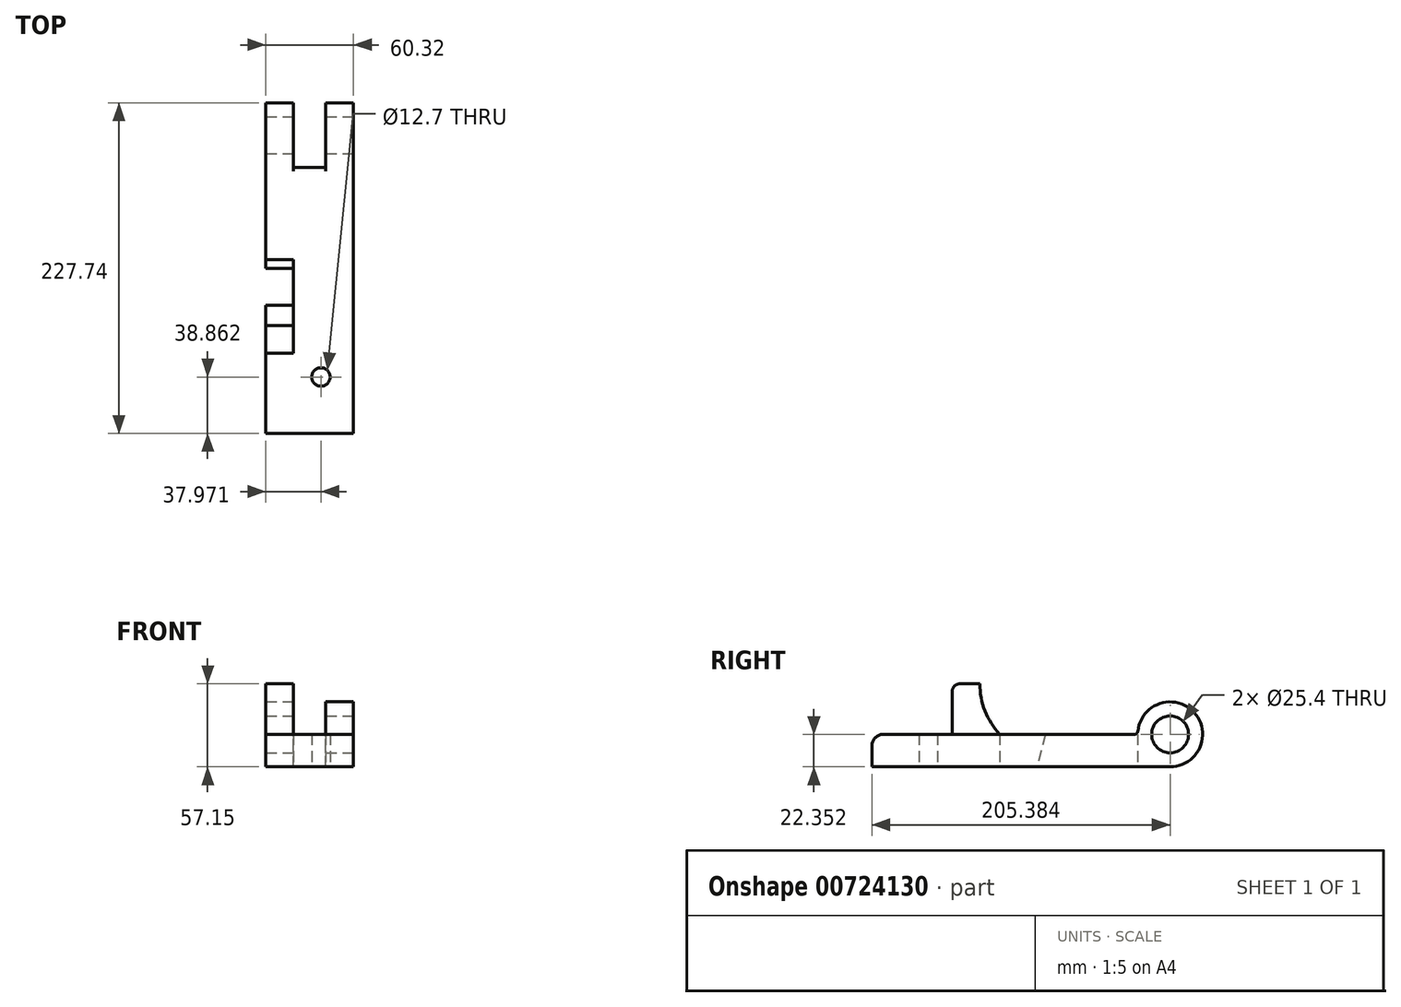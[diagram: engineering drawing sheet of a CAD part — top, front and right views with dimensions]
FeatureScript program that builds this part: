
annotation { "Feature Type Name" : "Feature", "Feature Type Description" : "" }
export const myFeature = defineFeature(function(context is Context, id is Id, definition is map)
    precondition{}
    {
        {
            var Q0;
            Q0=qCreatedBy(makeId("Top.planeOp"),FACE);
            var sketch = newSketch(context, id + "F0", { "sketchPlane" : qUnion([Q0])});
            skLineSegment(sketch, "E0.bottom", {"start": v(30.16, 97.1) * mm, "end": v(-30.16, 97.1) * mm});
            skLineSegment(sketch, "E0.top", {"start": v(30.16, -97.1) * mm, "end": v(-30.16, -97.1) * mm});
            skLineSegment(sketch, "E0.left", {"start": v(30.16, 97.1) * mm, "end": v(30.16, -97.1) * mm});
            skLineSegment(sketch, "E0.right", {"start": v(-30.16, 97.1) * mm, "end": v(-30.16, -97.1) * mm});
            skPoint(sketch, "E0.middle", {"position": v(0, 0) * mm});
            skLineSegment(sketch, "E1.bottom", {"start": v(30.16, 58.62) * mm, "end": v(-30.16, 58.62) * mm});
            skLineSegment(sketch, "E1.top", {"start": v(30.16, -58.62) * mm, "end": v(-30.16, -58.62) * mm});
            skLineSegment(sketch, "E1.left", {"start": v(30.16, 58.62) * mm, "end": v(30.16, -58.62) * mm});
            skLineSegment(sketch, "E1.right", {"start": v(-30.16, 58.62) * mm, "end": v(-30.16, -58.62) * mm});
            skLineSegment(sketch, "E2.bottom", {"start": v(30.16, 108.28) * mm, "end": v(-30.16, 108.28) * mm});
            skLineSegment(sketch, "E2.top", {"start": v(30.16, -108.28) * mm, "end": v(-30.16, -108.28) * mm});
            skLineSegment(sketch, "E2.left", {"start": v(30.16, 108.28) * mm, "end": v(30.16, -108.28) * mm});
            skLineSegment(sketch, "E2.right", {"start": v(-30.16, 108.28) * mm, "end": v(-30.16, -108.28) * mm});
            skCircle(sketch, "E3", {"center": v(7.81, -69.42) * mm, "radius": 6.35 * mm});
            skSolve(sketch);
        }
        {
            var Q0;
            {var subQ0=sQuery(id+"F0.wireOp",EDGE,"E0.top");Q0=makeQuery(id+"F0.imprint","IMPRINT",FACE,{"disambiguationData":[TD([[makeQuery(id+"F0.imprint","IMPRINT",EDGE,{"derivedFrom":subQ0}),1.0]])]});}
            var Q1;
            {var subQ0=sQuery(id+"F0.wireOp",EDGE,"E0.bottom");Q1=makeQuery(id+"F0.imprint","IMPRINT",FACE,{"disambiguationData":[TD([[makeQuery(id+"F0.imprint","IMPRINT",EDGE,{"derivedFrom":subQ0}),1.0]])]});}
            var Q2;
            {var subQ2=sQuery(id+"F0.wireOp",EDGE,"E0.top");Q2=makeQuery(id+"F0.imprint","IMPRINT",FACE,{"disambiguationData":[TD([[makeQuery(id+"F0.imprint","IMPRINT",EDGE,{"derivedFrom":subQ2}),-1.0]])]});}
            var Q3;
            {var subQ0=sQuery(id+"F0.wireOp",EDGE,"E1.bottom");Q3=makeQuery(id+"F0.imprint","IMPRINT",FACE,{"disambiguationData":[TD([[makeQuery(id+"F0.imprint","IMPRINT",EDGE,{"derivedFrom":subQ0}),1.0]])]});}
            extrude(context, id + "F1", {"entities" : qUnion([Q0, Q1, Q2, Q3]), "depth" : 22.35 * mm, "offsetDistance" : 25.4 * mm});
        }
        {
            var Q0;
            Q0=qCreatedBy(makeId("Right.planeOp"),FACE);
            var sketch = newSketch(context, id + "F2", { "sketchPlane" : qUnion([Q0])});
            skCircle(sketch, "E4", {"center": v(97.1, 22.35) * mm, "radius": 12.7 * mm});
            skCircle(sketch, "E5", {"center": v(97.1, 22.35) * mm, "radius": 22.35 * mm});
            skLineSegment(sketch, "E6.bottom", {"start": v(69.85, 67.28) * mm, "end": v(124.36, 67.28) * mm});
            skLineSegment(sketch, "E6.top", {"start": v(69.85, -22.58) * mm, "end": v(124.36, -22.58) * mm});
            skLineSegment(sketch, "E6.left", {"start": v(69.85, 67.28) * mm, "end": v(69.85, -22.58) * mm});
            skLineSegment(sketch, "E6.right", {"start": v(124.36, 67.28) * mm, "end": v(124.36, -22.58) * mm});
            skSolve(sketch);
        }
        {
            var Q0;
            Q0=makeQuery(id+"F2.imprint","IMPRINT",FACE,{"disambiguationData":[TD([[makeQuery(id+"F2.imprint","IMPRINT",EDGE,{"derivedFrom":sQuery(id+"F2.wireOp",EDGE,"E4")}),-1.0]])]});
            var Q1;
            Q1=makeQuery(id+"F1.opExtrude","SWEPT_FACE",FACE,{"disambiguationData":[OSD([sQuery(id+"F0.wireOp",EDGE,"E0.right"),sQuery(id+"F0.wireOp",EDGE,"E2.right")])]});
            extrude(context, id + "F3", {"entities" : qUnion([Q0]), "operationType" : NewBodyOperationType.ADD, "endBound" : BoundingType.UP_TO_SURFACE, "oppositeDirection" : true, "depth" : 60.7 * mm, "endBoundEntityFace" : qUnion([Q1]), "offsetDistance" : 25.4 * mm});
        }
        {
            var Q0;
            Q0=makeQuery(id+"F2.imprint","IMPRINT",FACE,{"disambiguationData":[TD([[makeQuery(id+"F2.imprint","IMPRINT",EDGE,{"derivedFrom":sQuery(id+"F2.wireOp",EDGE,"E4")}),-1.0]])]});
            var Q1;
            Q1=makeQuery(id+"F1.opExtrude","SWEPT_FACE",FACE,{"disambiguationData":[OSD([sQuery(id+"F0.wireOp",EDGE,"E0.left"),sQuery(id+"F0.wireOp",EDGE,"E2.left")])]});
            extrude(context, id + "F4", {"entities" : qUnion([Q0]), "operationType" : NewBodyOperationType.ADD, "endBound" : BoundingType.UP_TO_SURFACE, "depth" : 32.26 * mm, "endBoundEntityFace" : qUnion([Q1]), "offsetDistance" : 25.4 * mm});
        }
        {
            var Q0;
            Q0=makeQuery(id+"F2.imprint","IMPRINT",FACE,{"disambiguationData":[TD([[makeQuery(id+"F2.imprint","IMPRINT",EDGE,{"derivedFrom":sQuery(id+"F2.wireOp",EDGE,"E4")}),1.0]])]});
            extrude(context, id + "F5", {"entities" : qUnion([Q0]), "operationType" : NewBodyOperationType.REMOVE, "depth" : 88.65 * mm, "offsetDistance" : 25.4 * mm});
        }
        {
            var Q0;
            Q0=makeQuery(id+"F2.imprint","IMPRINT",FACE,{"disambiguationData":[TD([[makeQuery(id+"F2.imprint","IMPRINT",EDGE,{"derivedFrom":sQuery(id+"F2.wireOp",EDGE,"E4")}),1.0]])]});
            extrude(context, id + "F6", {"entities" : qUnion([Q0]), "operationType" : NewBodyOperationType.REMOVE, "oppositeDirection" : true, "depth" : 134.62 * mm, "offsetDistance" : 25.4 * mm});
        }
        {
            var Q0;
            Q0=qCreatedBy(makeId("Top.planeOp"),FACE);
            var sketch = newSketch(context, id + "F7", { "sketchPlane" : qUnion([Q0])});
            skLineSegment(sketch, "E7.bottom", {"start": v(11.16, 145.58) * mm, "end": v(-11.16, 145.58) * mm});
            skLineSegment(sketch, "E7.top", {"start": v(11.16, 74.75) * mm, "end": v(-11.16, 74.75) * mm});
            skLineSegment(sketch, "E7.left", {"start": v(11.16, 145.58) * mm, "end": v(11.16, 74.75) * mm});
            skLineSegment(sketch, "E7.right", {"start": v(-11.16, 145.58) * mm, "end": v(-11.16, 74.75) * mm});
            skPoint(sketch, "E7.middle", {"position": v(0, 110.17) * mm});
            skSolve(sketch);
        }
        {
            var Q0;
            Q0 = qSketchRegion(id + "F7", true);
            extrude(context, id + "F8", {"entities" : qUnion([Q0]), "operationType" : NewBodyOperationType.REMOVE, "depth" : 49.53 * mm, "offsetDistance" : 25.4 * mm});
        }
        {
            var Q0;
            Q0=makeQuery(id+"F3.boolean.opBoolean","MERGE",FACE,{"derivedFrom":[makeQuery(id+"F1.opExtrude","SWEPT_FACE",FACE,{"disambiguationData":[OSD([sQuery(id+"F0.wireOp",EDGE,"E0.right"),sQuery(id+"F0.wireOp",EDGE,"E2.right")])]}),makeQuery(id+"F3.opExtrude","CAP_FACE",FACE,{"disambiguationData":[OSD([sQuery(id+"F2.wireOp",EDGE,"E4"),sQuery(id+"F2.wireOp",EDGE,"E5")])],"isStart":false})]});
            var sketch = newSketch(context, id + "F9", { "sketchPlane" : qUnion([Q0])});
            skLineSegment(sketch, "E8", {"start": v(-182.96, 22.35) * mm, "end": v(-182.96, 22.35) * mm});
            skLineSegment(sketch, "E9", {"start": v(-11.25, 22.35) * mm, "end": v(-5.26, 0) * mm});
            skLineSegment(sketch, "E10", {"start": v(20.14, 22.35) * mm, "end": v(20.14, 0) * mm});
            skSolve(sketch);
        }
        {
            var Q0;
            {var subQ0=sQuery(id+"F9.wireOp",EDGE,"E9");Q0=makeQuery(id+"F9.imprint","IMPRINT",FACE,{"disambiguationData":[TD([[makeQuery(id+"F9.imprint","IMPRINT",EDGE,{"derivedFrom":subQ0}),1.0]])]});}
            extrude(context, id + "F10", {"entities" : qUnion([Q0]), "operationType" : NewBodyOperationType.REMOVE, "oppositeDirection" : true, "depth" : 19.05 * mm, "offsetDistance" : 25.4 * mm});
        }
        {
            var Q0;
            Q0=makeQuery(id+"F1.opExtrude","CAP_EDGE",EDGE,{"disambiguationData":[OSD([sQuery(id+"F0.wireOp",EDGE,"E2.top")])],"isStart":false});
            fillet(context, id + "F11", {"entities" : qUnion([Q0]), "radius" : 7.87 * mm, "tangentPropagation" : true, "allowEdgeOverflow" : false});
        }
        {
            var Q0;
            {var subQ0=sQuery(id+"F9.wireOp",EDGE,"E10");Q0=makeQuery(id+"F9.imprint","IMPRINT",FACE,{"disambiguationData":[TD([[makeQuery(id+"F9.imprint","IMPRINT",EDGE,{"derivedFrom":subQ0}),1.0]])]});}
            var sketch = newSketch(context, id + "F12", { "sketchPlane" : qUnion([Q0])});
            skLineSegment(sketch, "E11", {"start": v(52.98, 22.35) * mm, "end": v(52.98, 57.15) * mm});
            skLineSegment(sketch, "E12", {"start": v(52.98, 57.15) * mm, "end": v(33.93, 57.15) * mm});
            skPoint(sketch, "E13", {"position": v(20.14, 22.35) * mm});
            skArc(sketch, "E14", {"start": v(20.14, 22.35) * mm, "mid": v(30.36, 38.43) * mm, "end": v(33.93, 57.15) * mm});
            skSolve(sketch);
        }
        {
            var Q0;
            {var subQ0=sQuery(id+"F12.wireOp",EDGE,"E11");Q0=makeQuery(id+"F12.imprint","IMPRINT",FACE,{"disambiguationData":[TD([[makeQuery(id+"F12.imprint","IMPRINT",EDGE,{"derivedFrom":subQ0}),1.0]])]});}
            extrude(context, id + "F13", {"entities" : qUnion([Q0]), "operationType" : NewBodyOperationType.ADD, "oppositeDirection" : true, "depth" : 19.05 * mm, "offsetDistance" : 25.4 * mm});
        }
        {
            var Q0;
            {var subQ0=sQuery(id+"F2.wireOp",EDGE,"E5");var subQ1=makeQuery(id+"F3.opExtrude","SWEPT_FACE",FACE,{"disambiguationData":[OSD([subQ0])]});var subQ2=sQuery(id+"F0.wireOp",EDGE,"E2.right");var subQ3=sQuery(id+"F0.wireOp",EDGE,"E0.right");var subQ4=makeQuery(id+"F1.opExtrude","CAP_FACE",FACE,{"disambiguationData":[OSD([sQuery(id+"F0.wireOp",EDGE,"E0.bottom"),sQuery(id+"F0.wireOp",EDGE,"E0.left"),subQ3,sQuery(id+"F0.wireOp",EDGE,"E2.top"),sQuery(id+"F0.wireOp",EDGE,"E2.left"),subQ2,sQuery(id+"F0.wireOp",EDGE,"E3")])],"isStart":false});var subQ5=makeQuery(id+"F4.opExtrude","SWEPT_FACE",FACE,{"disambiguationData":[OSD([subQ0])]});Q0=makeQuery(id+"F8.boolean.opBoolean","SPLIT",EDGE,{"disambiguationData":[topologyDisambiguationEdgeConnected([subQ4,subQ1,subQ5]),TD([makeQuery(id+"F8.opExtrude","SWEPT_FACE",FACE,{"disambiguationData":[OSD([sQuery(id+"F7.wireOp",EDGE,"E7.right")])]})])],"derivedFrom":makeQuery(id+"F4.boolean.opBoolean","INTERSECT",EDGE,{"derivedFrom":[subQ4,subQ5]})});}
            var Q1;
            {var subQ0=sQuery(id+"F2.wireOp",EDGE,"E5");var subQ1=makeQuery(id+"F3.opExtrude","SWEPT_FACE",FACE,{"disambiguationData":[OSD([subQ0])]});var subQ2=sQuery(id+"F0.wireOp",EDGE,"E2.left");var subQ3=sQuery(id+"F0.wireOp",EDGE,"E0.left");var subQ4=makeQuery(id+"F1.opExtrude","CAP_FACE",FACE,{"disambiguationData":[OSD([sQuery(id+"F0.wireOp",EDGE,"E0.bottom"),subQ3,sQuery(id+"F0.wireOp",EDGE,"E0.right"),sQuery(id+"F0.wireOp",EDGE,"E2.top"),subQ2,sQuery(id+"F0.wireOp",EDGE,"E2.right"),sQuery(id+"F0.wireOp",EDGE,"E3")])],"isStart":false});var subQ5=makeQuery(id+"F4.opExtrude","SWEPT_FACE",FACE,{"disambiguationData":[OSD([subQ0])]});Q1=makeQuery(id+"F8.boolean.opBoolean","SPLIT",EDGE,{"disambiguationData":[topologyDisambiguationEdgeConnected([subQ4,subQ1,subQ5]),TD([makeQuery(id+"F8.opExtrude","SWEPT_FACE",FACE,{"disambiguationData":[OSD([sQuery(id+"F7.wireOp",EDGE,"E7.left")])]})])],"derivedFrom":makeQuery(id+"F4.boolean.opBoolean","INTERSECT",EDGE,{"derivedFrom":[subQ4,subQ5]})});}
            var Q2;
            Q2=makeQuery(id+"F13.opExtrude","SWEPT_EDGE",EDGE,{"disambiguationData":[OSD([sQuery(id+"F0.wireOp",EDGE,"E0.right"),sQuery(id+"F0.wireOp",EDGE,"E2.right"),sQuery(id+"F12.wireOp",EDGE,"E11")])]});
            fillet(context, id + "F14", {"entities" : qUnion([Q0, Q1, Q2]), "radius" : 2.54 * mm, "tangentPropagation" : true, "allowEdgeOverflow" : false});
        }
        {
            var Q0;
            Q0=makeQuery(id+"F13.opExtrude","SWEPT_EDGE",EDGE,{"disambiguationData":[OSD([sQuery(id+"F12.wireOp",EDGE,"E11"),sQuery(id+"F12.wireOp",EDGE,"E12")])]});
            fillet(context, id + "F15", {"entities" : qUnion([Q0]), "radius" : 5.08 * mm, "tangentPropagation" : true, "allowEdgeOverflow" : false});
        }
    });
